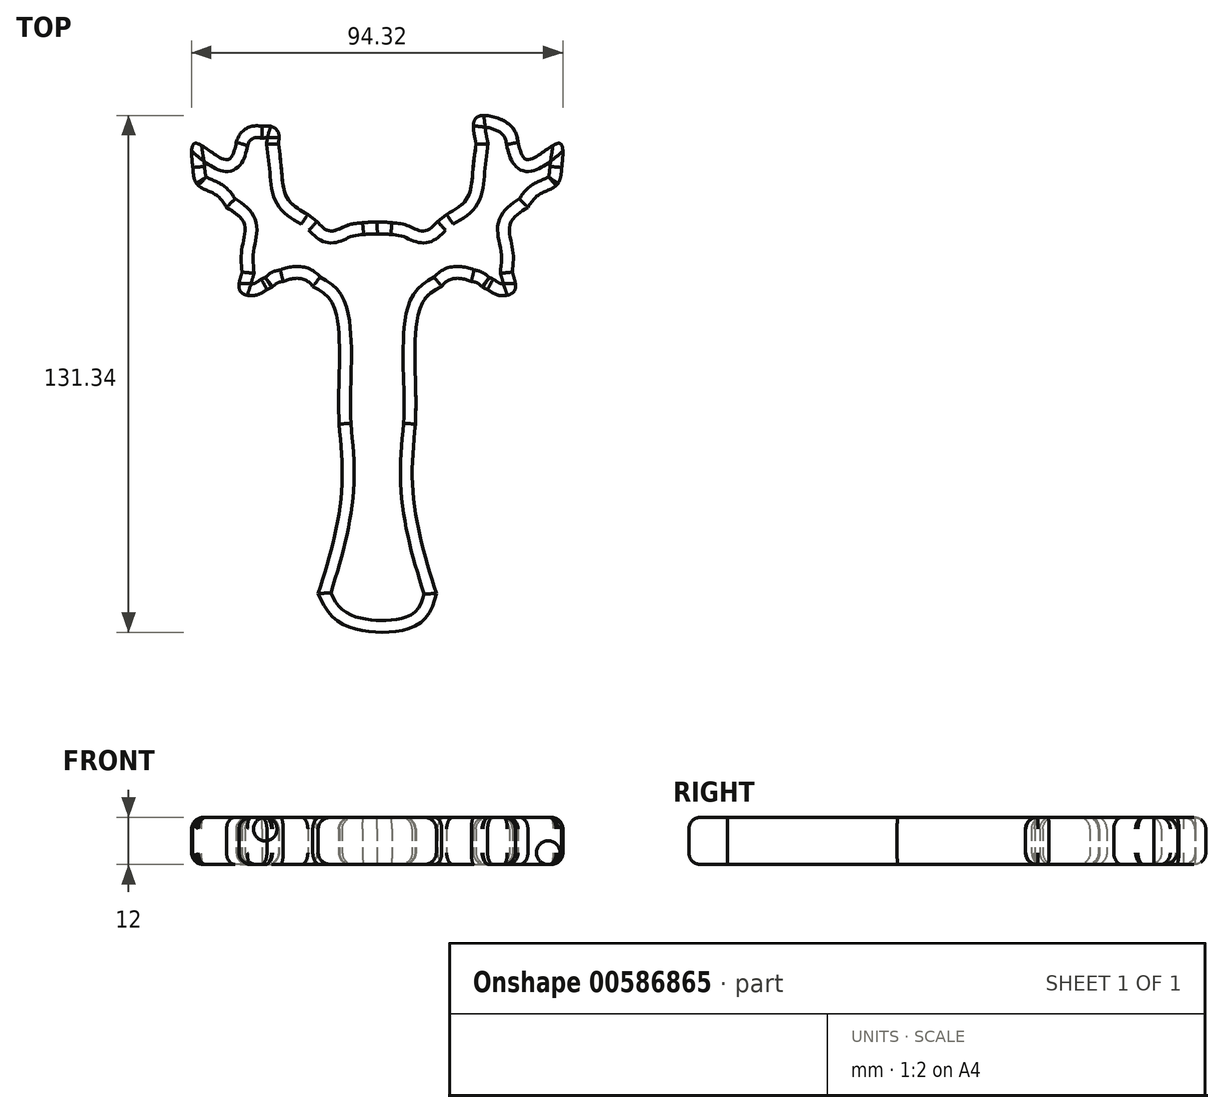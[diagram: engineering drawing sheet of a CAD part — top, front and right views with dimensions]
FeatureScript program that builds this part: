
annotation { "Feature Type Name" : "Feature", "Feature Type Description" : "" }
export const myFeature = defineFeature(function(context is Context, id is Id, definition is map)
    precondition{}
    {
        {
            var Q0;
            Q0=qCreatedBy(makeId("Top.planeOp"),FACE);
            var sketch = newSketch(context, id + "F0", { "sketchPlane" : qUnion([Q0])});
            skFitSpline(sketch, "E0", {"points": [v(-29.26, 62.36) * mm, v(-31.72, 62.38) * mm, v(-34.58, 60.72) * mm, v(-35.8, 58.28) * mm]});
            skFitSpline(sketch, "E1", {"points": [v(-35.8, 58.28) * mm, v(-38.4, 53.87) * mm, v(-46.17, 58.05) * mm, v(-46.86, 51.88) * mm]});
            skFitSpline(sketch, "E2", {"points": [v(-46.86, 51.88) * mm, v(-45.62, 47.43) * mm, v(-41.15, 45.05) * mm, v(-38.27, 41.74) * mm]});
            skFitSpline(sketch, "E3", {"points": [v(-38.27, 41.74) * mm, v(-33.76, 37.52) * mm, v(-34.43, 30.94) * mm, v(-34.31, 25.31) * mm]});
            skFitSpline(sketch, "E4", {"points": [v(-34.31, 25.31) * mm, v(-34.8, 20.47) * mm, v(-31.15, 19.37) * mm, v(-28.04, 20.88) * mm]});
            skFitSpline(sketch, "E5", {"points": [v(-28.04, 20.88) * mm, v(-26.69, 21.54) * mm, v(-25.5, 22.5) * mm, v(-23.9, 22.94) * mm]});
            skFitSpline(sketch, "E6", {"points": [v(-23.9, 22.94) * mm, v(-20.8, 23.73) * mm, v(-18.03, 23.2) * mm, v(-16.39, 21.66) * mm]});
            skFitSpline(sketch, "E7", {"points": [v(-16.39, 21.66) * mm, v(-11.07, 16.68) * mm, v(-9.77, -4.68) * mm, v(-9.7, -13.3) * mm]});
            skFitSpline(sketch, "E8", {"points": [v(-9.7, -13.3) * mm, v(-8.91, -27.85) * mm, v(-11, -42.41) * mm, v(-15, -56.38) * mm]});
            skFitSpline(sketch, "E9", {"points": [v(-15, -56.38) * mm, v(-8.4, -64.33) * mm, v(10.12, -64.4) * mm, v(15, -56.38) * mm]});
            skFitSpline(sketch, "E10", {"points": [v(15, -56.38) * mm, v(11, -42.41) * mm, v(8.91, -27.85) * mm, v(9.7, -13.3) * mm]});
            skFitSpline(sketch, "E11", {"points": [v(9.7, -13.3) * mm, v(9.77, -4.68) * mm, v(11.07, 16.68) * mm, v(16.39, 21.66) * mm]});
            skFitSpline(sketch, "E12", {"points": [v(16.39, 21.66) * mm, v(18.03, 23.2) * mm, v(20.8, 23.73) * mm, v(23.9, 22.94) * mm]});
            skFitSpline(sketch, "E13", {"points": [v(23.9, 22.94) * mm, v(25.5, 22.5) * mm, v(26.69, 21.54) * mm, v(28.04, 20.88) * mm]});
            skFitSpline(sketch, "E14", {"points": [v(28.04, 20.88) * mm, v(31.15, 19.37) * mm, v(34.8, 20.47) * mm, v(34.31, 25.31) * mm]});
            skFitSpline(sketch, "E15", {"points": [v(34.31, 25.31) * mm, v(34.43, 30.94) * mm, v(33.76, 37.52) * mm, v(38.27, 41.74) * mm]});
            skFitSpline(sketch, "E16", {"points": [v(38.27, 41.74) * mm, v(41.15, 45.05) * mm, v(45.62, 47.43) * mm, v(46.86, 51.88) * mm]});
            skFitSpline(sketch, "E17", {"points": [v(46.86, 51.88) * mm, v(46.17, 58.05) * mm, v(38.4, 53.87) * mm, v(35.8, 58.28) * mm]});
            skFitSpline(sketch, "E18", {"points": [v(35.8, 58.28) * mm, v(33.5, 62.87) * mm, v(25.37, 64.7) * mm, v(25.12, 57.8) * mm]});
            skFitSpline(sketch, "E19", {"points": [v(25.12, 57.8) * mm, v(24.33, 51.42) * mm, v(22.86, 44.16) * mm, v(17.63, 39.96) * mm]});
            skLineSegment(sketch, "E20", {"start": v(17.63, 39.96) * mm, "end": v(15.35, 38.13) * mm});
            skFitSpline(sketch, "E21", {"points": [v(15.35, 38.13) * mm, v(11.94, 35.75) * mm, v(7.64, 37.17) * mm, v(3.73, 37.83) * mm]});
            skFitSpline(sketch, "E22", {"points": [v(3.73, 37.83) * mm, v(2.5, 37.96) * mm, v(1.24, 38.02) * mm, v(0, 38.03) * mm]});
            skFitSpline(sketch, "E23", {"points": [v(0, 38.03) * mm, v(-1.29, 38) * mm, v(-2.62, 37.95) * mm, v(-3.73, 37.83) * mm]});
            skFitSpline(sketch, "E24", {"points": [v(-3.73, 37.83) * mm, v(-7.64, 37.17) * mm, v(-11.94, 35.75) * mm, v(-15.35, 38.13) * mm]});
            skLineSegment(sketch, "E25", {"start": v(-15.35, 38.13) * mm, "end": v(-17.63, 39.96) * mm});
            skFitSpline(sketch, "E26", {"points": [v(-17.63, 39.96) * mm, v(-22.86, 44.16) * mm, v(-24.34, 51.42) * mm, v(-25.12, 57.8) * mm]});
            skFitSpline(sketch, "E27", {"points": [v(-25.12, 57.8) * mm, v(-25.24, 61.03) * mm, v(-27.09, 62.35) * mm, v(-29.26, 62.36) * mm]});
            skLineSegment(sketch, "E28", {"start": v(-29.26, 62.36) * mm, "end": v(-29.26, 62.36) * mm});
            skSolve(sketch);
        }
        {
            var Q0;
            Q0=makeQuery(id+"F0.imprint","IMPRINT",FACE,{"disambiguationData":[TD([[makeQuery(id+"F0.imprint","IMPRINT",EDGE,{"derivedFrom":sQuery(id+"F0.wireOp",EDGE,"E0")}),1.0]])]});
            extrude(context, id + "F1", {"entities" : qUnion([Q0]), "depth" : 12 * mm, "offsetDistance" : 25 * mm});
        }
        {
            var Q0;
            Q0=makeQuery(id+"F1.opExtrude","CAP_EDGE",EDGE,{"disambiguationData":[OSD([sQuery(id+"F0.wireOp",EDGE,"E8")])],"isStart":false});
            var Q1;
            Q1=makeQuery(id+"F1.opExtrude","CAP_EDGE",EDGE,{"disambiguationData":[OSD([sQuery(id+"F0.wireOp",EDGE,"E7")])],"isStart":false});
            var Q2;
            Q2=makeQuery(id+"F1.opExtrude","CAP_EDGE",EDGE,{"disambiguationData":[OSD([sQuery(id+"F0.wireOp",EDGE,"E9")])],"isStart":false});
            var Q3;
            Q3=makeQuery(id+"F1.opExtrude","CAP_EDGE",EDGE,{"disambiguationData":[OSD([sQuery(id+"F0.wireOp",EDGE,"E10")])],"isStart":false});
            var Q4;
            Q4=makeQuery(id+"F1.opExtrude","CAP_EDGE",EDGE,{"disambiguationData":[OSD([sQuery(id+"F0.wireOp",EDGE,"E11")])],"isStart":false});
            var Q5;
            Q5=makeQuery(id+"F1.opExtrude","CAP_EDGE",EDGE,{"disambiguationData":[OSD([sQuery(id+"F0.wireOp",EDGE,"E12")])],"isStart":false});
            var Q6;
            Q6=makeQuery(id+"F1.opExtrude","CAP_EDGE",EDGE,{"disambiguationData":[OSD([sQuery(id+"F0.wireOp",EDGE,"E13")])],"isStart":false});
            var Q7;
            Q7=makeQuery(id+"F1.opExtrude","CAP_EDGE",EDGE,{"disambiguationData":[OSD([sQuery(id+"F0.wireOp",EDGE,"E15")])],"isStart":false});
            var Q8;
            Q8=makeQuery(id+"F1.opExtrude","CAP_EDGE",EDGE,{"disambiguationData":[OSD([sQuery(id+"F0.wireOp",EDGE,"E14")])],"isStart":false});
            var Q9;
            Q9=makeQuery(id+"F1.opExtrude","CAP_EDGE",EDGE,{"disambiguationData":[OSD([sQuery(id+"F0.wireOp",EDGE,"E18")])],"isStart":false});
            var Q10;
            Q10=makeQuery(id+"F1.opExtrude","CAP_EDGE",EDGE,{"disambiguationData":[OSD([sQuery(id+"F0.wireOp",EDGE,"E20")])],"isStart":false});
            var Q11;
            Q11=makeQuery(id+"F1.opExtrude","CAP_EDGE",EDGE,{"disambiguationData":[OSD([sQuery(id+"F0.wireOp",EDGE,"E21")])],"isStart":false});
            var Q12;
            Q12=makeQuery(id+"F1.opExtrude","CAP_EDGE",EDGE,{"disambiguationData":[OSD([sQuery(id+"F0.wireOp",EDGE,"E22")])],"isStart":false});
            var Q13;
            Q13=makeQuery(id+"F1.opExtrude","CAP_EDGE",EDGE,{"disambiguationData":[OSD([sQuery(id+"F0.wireOp",EDGE,"E24")])],"isStart":false});
            var Q14;
            Q14=makeQuery(id+"F1.opExtrude","CAP_EDGE",EDGE,{"disambiguationData":[OSD([sQuery(id+"F0.wireOp",EDGE,"E25")])],"isStart":false});
            var Q15;
            Q15=makeQuery(id+"F1.opExtrude","CAP_EDGE",EDGE,{"disambiguationData":[OSD([sQuery(id+"F0.wireOp",EDGE,"E26")])],"isStart":false});
            var Q16;
            Q16=makeQuery(id+"F1.opExtrude","CAP_EDGE",EDGE,{"disambiguationData":[OSD([sQuery(id+"F0.wireOp",EDGE,"E27")])],"isStart":false});
            var Q17;
            Q17=makeQuery(id+"F1.opExtrude","CAP_EDGE",EDGE,{"disambiguationData":[OSD([sQuery(id+"F0.wireOp",EDGE,"E3")])],"isStart":false});
            var Q18;
            Q18=makeQuery(id+"F1.opExtrude","CAP_EDGE",EDGE,{"disambiguationData":[OSD([sQuery(id+"F0.wireOp",EDGE,"E2")])],"isStart":false});
            var Q19;
            Q19=makeQuery(id+"F1.opExtrude","CAP_EDGE",EDGE,{"disambiguationData":[OSD([sQuery(id+"F0.wireOp",EDGE,"E4")])],"isStart":false});
            var Q20;
            Q20=makeQuery(id+"F1.opExtrude","CAP_EDGE",EDGE,{"disambiguationData":[OSD([sQuery(id+"F0.wireOp",EDGE,"E6")])],"isStart":false});
            var Q21;
            Q21=makeQuery(id+"F1.opExtrude","CAP_EDGE",EDGE,{"disambiguationData":[OSD([sQuery(id+"F0.wireOp",EDGE,"E16")])],"isStart":false});
            var Q22;
            Q22=makeQuery(id+"F1.opExtrude","CAP_EDGE",EDGE,{"disambiguationData":[OSD([sQuery(id+"F0.wireOp",EDGE,"E19")])],"isStart":false});
            var Q23;
            Q23=makeQuery(id+"F1.opExtrude","CAP_EDGE",EDGE,{"disambiguationData":[OSD([sQuery(id+"F0.wireOp",EDGE,"E0")])],"isStart":false});
            var Q24;
            Q24=makeQuery(id+"F1.opExtrude","CAP_EDGE",EDGE,{"disambiguationData":[OSD([sQuery(id+"F0.wireOp",EDGE,"E1")])],"isStart":false});
            var Q25;
            Q25=makeQuery(id+"F1.opExtrude","CAP_EDGE",EDGE,{"disambiguationData":[OSD([sQuery(id+"F0.wireOp",EDGE,"E23")])],"isStart":false});
            var Q26;
            Q26=makeQuery(id+"F1.opExtrude","CAP_EDGE",EDGE,{"disambiguationData":[OSD([sQuery(id+"F0.wireOp",EDGE,"E5")])],"isStart":false});
            var Q27;
            Q27=makeQuery(id+"F1.opExtrude","CAP_EDGE",EDGE,{"disambiguationData":[OSD([sQuery(id+"F0.wireOp",EDGE,"E17")])],"isStart":false});
            fillet(context, id + "F2", {"entities" : qUnion([Q0, Q1, Q2, Q3, Q4, Q5, Q6, Q7, Q8, Q9, Q10, Q11, Q12, Q13, Q14, Q15, Q16, Q17, Q18, Q19, Q20, Q21, Q22, Q23, Q24, Q25, Q26, Q27]), "radius" : 3 * mm, "tangentPropagation" : true, "allowEdgeOverflow" : false});
        }
        {
            var Q0;
            Q0=makeQuery(id+"F1.opExtrude","CAP_EDGE",EDGE,{"disambiguationData":[OSD([sQuery(id+"F0.wireOp",EDGE,"E9")])],"isStart":true});
            var Q1;
            Q1=makeQuery(id+"F1.opExtrude","CAP_EDGE",EDGE,{"disambiguationData":[OSD([sQuery(id+"F0.wireOp",EDGE,"E8")])],"isStart":true});
            var Q2;
            Q2=makeQuery(id+"F1.opExtrude","CAP_EDGE",EDGE,{"disambiguationData":[OSD([sQuery(id+"F0.wireOp",EDGE,"E7")])],"isStart":true});
            var Q3;
            Q3=makeQuery(id+"F1.opExtrude","CAP_EDGE",EDGE,{"disambiguationData":[OSD([sQuery(id+"F0.wireOp",EDGE,"E6")])],"isStart":true});
            var Q4;
            Q4=makeQuery(id+"F1.opExtrude","CAP_EDGE",EDGE,{"disambiguationData":[OSD([sQuery(id+"F0.wireOp",EDGE,"E5")])],"isStart":true});
            var Q5;
            Q5=makeQuery(id+"F1.opExtrude","CAP_EDGE",EDGE,{"disambiguationData":[OSD([sQuery(id+"F0.wireOp",EDGE,"E4")])],"isStart":true});
            var Q6;
            Q6=makeQuery(id+"F1.opExtrude","CAP_EDGE",EDGE,{"disambiguationData":[OSD([sQuery(id+"F0.wireOp",EDGE,"E3")])],"isStart":true});
            var Q7;
            Q7=makeQuery(id+"F1.opExtrude","CAP_EDGE",EDGE,{"disambiguationData":[OSD([sQuery(id+"F0.wireOp",EDGE,"E2")])],"isStart":true});
            var Q8;
            Q8=makeQuery(id+"F1.opExtrude","CAP_EDGE",EDGE,{"disambiguationData":[OSD([sQuery(id+"F0.wireOp",EDGE,"E1")])],"isStart":true});
            var Q9;
            Q9=makeQuery(id+"F1.opExtrude","CAP_EDGE",EDGE,{"disambiguationData":[OSD([sQuery(id+"F0.wireOp",EDGE,"E0")])],"isStart":true});
            var Q10;
            Q10=makeQuery(id+"F1.opExtrude","CAP_EDGE",EDGE,{"disambiguationData":[OSD([sQuery(id+"F0.wireOp",EDGE,"E26")])],"isStart":true});
            var Q11;
            Q11=makeQuery(id+"F1.opExtrude","CAP_EDGE",EDGE,{"disambiguationData":[OSD([sQuery(id+"F0.wireOp",EDGE,"E25")])],"isStart":true});
            var Q12;
            Q12=makeQuery(id+"F1.opExtrude","CAP_EDGE",EDGE,{"disambiguationData":[OSD([sQuery(id+"F0.wireOp",EDGE,"E24")])],"isStart":true});
            var Q13;
            Q13=makeQuery(id+"F1.opExtrude","CAP_EDGE",EDGE,{"disambiguationData":[OSD([sQuery(id+"F0.wireOp",EDGE,"E23")])],"isStart":true});
            var Q14;
            Q14=makeQuery(id+"F1.opExtrude","CAP_EDGE",EDGE,{"disambiguationData":[OSD([sQuery(id+"F0.wireOp",EDGE,"E22")])],"isStart":true});
            var Q15;
            Q15=makeQuery(id+"F1.opExtrude","CAP_EDGE",EDGE,{"disambiguationData":[OSD([sQuery(id+"F0.wireOp",EDGE,"E21")])],"isStart":true});
            var Q16;
            Q16=makeQuery(id+"F1.opExtrude","CAP_EDGE",EDGE,{"disambiguationData":[OSD([sQuery(id+"F0.wireOp",EDGE,"E19")])],"isStart":true});
            var Q17;
            Q17=makeQuery(id+"F1.opExtrude","CAP_EDGE",EDGE,{"disambiguationData":[OSD([sQuery(id+"F0.wireOp",EDGE,"E20")])],"isStart":true});
            var Q18;
            Q18=makeQuery(id+"F1.opExtrude","CAP_EDGE",EDGE,{"disambiguationData":[OSD([sQuery(id+"F0.wireOp",EDGE,"E18")])],"isStart":true});
            var Q19;
            Q19=makeQuery(id+"F1.opExtrude","CAP_EDGE",EDGE,{"disambiguationData":[OSD([sQuery(id+"F0.wireOp",EDGE,"E17")])],"isStart":true});
            var Q20;
            Q20=makeQuery(id+"F1.opExtrude","CAP_EDGE",EDGE,{"disambiguationData":[OSD([sQuery(id+"F0.wireOp",EDGE,"E16")])],"isStart":true});
            var Q21;
            Q21=makeQuery(id+"F1.opExtrude","CAP_EDGE",EDGE,{"disambiguationData":[OSD([sQuery(id+"F0.wireOp",EDGE,"E14")])],"isStart":true});
            var Q22;
            Q22=makeQuery(id+"F1.opExtrude","CAP_EDGE",EDGE,{"disambiguationData":[OSD([sQuery(id+"F0.wireOp",EDGE,"E15")])],"isStart":true});
            var Q23;
            Q23=makeQuery(id+"F1.opExtrude","CAP_EDGE",EDGE,{"disambiguationData":[OSD([sQuery(id+"F0.wireOp",EDGE,"E27")])],"isStart":true});
            var Q24;
            Q24=makeQuery(id+"F1.opExtrude","CAP_EDGE",EDGE,{"disambiguationData":[OSD([sQuery(id+"F0.wireOp",EDGE,"E13")])],"isStart":true});
            var Q25;
            Q25=makeQuery(id+"F1.opExtrude","CAP_EDGE",EDGE,{"disambiguationData":[OSD([sQuery(id+"F0.wireOp",EDGE,"E12")])],"isStart":true});
            var Q26;
            Q26=makeQuery(id+"F1.opExtrude","CAP_EDGE",EDGE,{"disambiguationData":[OSD([sQuery(id+"F0.wireOp",EDGE,"E11")])],"isStart":true});
            var Q27;
            Q27=makeQuery(id+"F1.opExtrude","CAP_EDGE",EDGE,{"disambiguationData":[OSD([sQuery(id+"F0.wireOp",EDGE,"E10")])],"isStart":true});
            fillet(context, id + "F3", {"entities" : qUnion([Q0, Q1, Q2, Q3, Q4, Q5, Q6, Q7, Q8, Q9, Q10, Q11, Q12, Q13, Q14, Q15, Q16, Q17, Q18, Q19, Q20, Q21, Q22, Q23, Q24, Q25, Q26, Q27]), "radius" : 3 * mm, "tangentPropagation" : true, "allowEdgeOverflow" : false});
        }
    });
